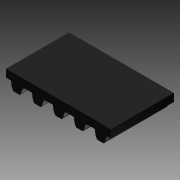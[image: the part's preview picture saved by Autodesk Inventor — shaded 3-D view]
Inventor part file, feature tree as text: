
AUTODESK INVENTOR PART (.ipt)
format: ipt  version: 2011 (Build 150239000, 239)  size: 138,240 bytes
history: native  units: in
note: dims shown in document units (in); Inventor stores cm internally (conversion verified against a paired STEP export)
features: extrude x1, sketch x1
ambient origin geometry x8: Origin, YZ Plane, XZ Plane, XY Plane, X Axis, Y Axis, Z Axis, Center Point
bodies: Solid1 (feature_tree)
feature tree (2):
  extrude  "Extrusion1"  Depth=0.1969in
  sketch  "Sketch1"  dims[d0=0.5906in d1=0.0in d2=0.1969in d3=0.15in d4=0.076in]
